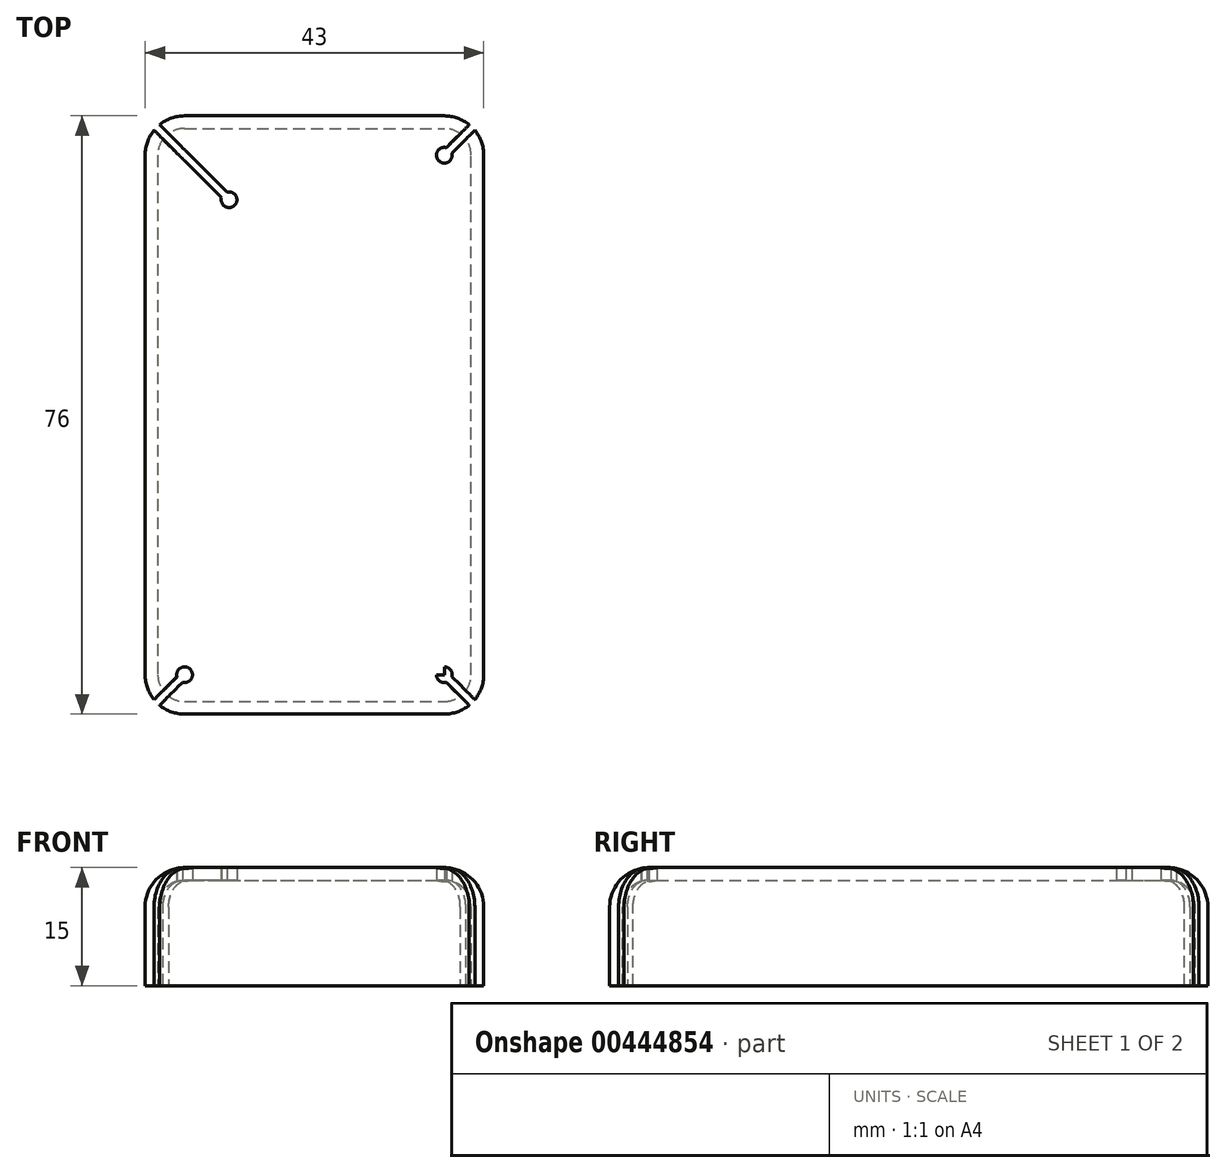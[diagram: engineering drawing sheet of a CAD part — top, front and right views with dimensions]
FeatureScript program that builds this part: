
annotation { "Feature Type Name" : "Feature", "Feature Type Description" : "" }
export const myFeature = defineFeature(function(context is Context, id is Id, definition is map)
    precondition{}
    {
        {
            var Q0;
            Q0=qCreatedBy(makeId("Top.planeOp"),FACE);
            var sketch = newSketch(context, id + "F0", { "sketchPlane" : qUnion([Q0])});
            skLineSegment(sketch, "E0.bottom", {"start": v(-21.5, 38) * mm, "end": v(21.5, 38) * mm});
            skLineSegment(sketch, "E0.top", {"start": v(-21.5, -38) * mm, "end": v(21.5, -38) * mm});
            skLineSegment(sketch, "E0.left", {"start": v(-21.5, 38) * mm, "end": v(-21.5, -38) * mm});
            skLineSegment(sketch, "E0.right", {"start": v(21.5, 38) * mm, "end": v(21.5, -38) * mm});
            skPoint(sketch, "E0.middle", {"position": v(0, 0) * mm});
            skSolve(sketch);
        }
        {
            var Q0;
            Q0=qSketchRegion(id+"F0",true);
            extrude(context, id + "F1", {"entities" : qUnion([Q0]), "depth" : 15 * mm});
        }
        {
            var Q0;
            Q0=makeQuery(id+"F1.opExtrude","SWEPT_EDGE",EDGE,{"disambiguationData":[OSD([sQuery(id+"F0.wireOp",EDGE,"E0.top"),sQuery(id+"F0.wireOp",EDGE,"E0.left")])]});
            var Q1;
            Q1=makeQuery(id+"F1.opExtrude","SWEPT_EDGE",EDGE,{"disambiguationData":[OSD([sQuery(id+"F0.wireOp",EDGE,"E0.top"),sQuery(id+"F0.wireOp",EDGE,"E0.right")])]});
            var Q2;
            Q2=makeQuery(id+"F1.opExtrude","SWEPT_EDGE",EDGE,{"disambiguationData":[OSD([sQuery(id+"F0.wireOp",EDGE,"E0.bottom"),sQuery(id+"F0.wireOp",EDGE,"E0.right")])]});
            var Q3;
            Q3=makeQuery(id+"F1.opExtrude","SWEPT_EDGE",EDGE,{"disambiguationData":[OSD([sQuery(id+"F0.wireOp",EDGE,"E0.bottom"),sQuery(id+"F0.wireOp",EDGE,"E0.left")])]});
            var Q4;
            Q4=makeQuery(id+"F1.opExtrude","CAP_FACE",FACE,{"disambiguationData":[OSD([sQuery(id+"F0.wireOp",EDGE,"E0.bottom"),sQuery(id+"F0.wireOp",EDGE,"E0.top"),sQuery(id+"F0.wireOp",EDGE,"E0.left"),sQuery(id+"F0.wireOp",EDGE,"E0.right")])],"isStart":false});
            fillet(context, id + "F2", {"entities" : qUnion([Q0, Q1, Q2, Q3, Q4]), "radius" : 5 * mm, "tangentPropagation" : true, "allowEdgeOverflow" : false});
        }
        {
            var Q0;
            Q0=makeQuery(id+"F1.opExtrude","CAP_FACE",FACE,{"disambiguationData":[OSD([sQuery(id+"F0.wireOp",EDGE,"E0.bottom"),sQuery(id+"F0.wireOp",EDGE,"E0.top"),sQuery(id+"F0.wireOp",EDGE,"E0.left"),sQuery(id+"F0.wireOp",EDGE,"E0.right")])],"isStart":true});
            shell(context, id + "F3", {"entities" : qUnion([Q0]), "thickness" : 1.6 * mm});
        }
        {
            var Q0;
            Q0=qCreatedBy(makeId("Top.planeOp"),FACE);
            var sketch = newSketch(context, id + "F4", { "sketchPlane" : qUnion([Q0])});
            skLineSegment(sketch, "E1.0.0", {"start": v(-16.5, -33) * mm, "end": v(16.5, -33) * mm});
            skLineSegment(sketch, "E1.0.1", {"start": v(16.5, -33) * mm, "end": v(16.5, 33) * mm});
            skLineSegment(sketch, "E1.0.2", {"start": v(16.5, 33) * mm, "end": v(-16.5, 33) * mm});
            skLineSegment(sketch, "E1.0.3", {"start": v(-16.5, 33) * mm, "end": v(-16.5, -33) * mm});
            skCircle(sketch, "E2", {"center": v(-16.5, -33) * mm, "radius": 1 * mm});
            skCircle(sketch, "E3", {"center": v(16.5, 33) * mm, "radius": 1 * mm});
            skCircle(sketch, "E4", {"center": v(16.5, -33) * mm, "radius": 1 * mm});
            skLineSegment(sketch, "E5", {"start": v(-16.5, 33) * mm, "end": v(-10.84, 27.34) * mm});
            skCircle(sketch, "E6", {"center": v(-10.84, 27.34) * mm, "radius": 1 * mm});
            skPoint(sketch, "E7.0", {"position": v(20.04, 36.54) * mm});
            skLineSegment(sketch, "E8", {"start": v(16.5, 33) * mm, "end": v(20.04, 36.54) * mm});
            skLineSegment(sketch, "E9", {"start": v(20.04, 36.54) * mm, "end": v(19.68, 36.89) * mm});
            skLineSegment(sketch, "E10", {"start": v(19.68, 36.89) * mm, "end": v(15.63, 32.84) * mm});
            skLineSegment(sketch, "E11", {"start": v(20.04, 36.54) * mm, "end": v(20.39, 36.18) * mm});
            skLineSegment(sketch, "E12", {"start": v(20.39, 36.18) * mm, "end": v(16.51, 32.3) * mm});
            skLineSegment(sketch, "E13", {"start": v(16.5, 33) * mm, "end": v(16.85, 32.65) * mm});
            skLineSegment(sketch, "E14", {"start": v(16.5, 33) * mm, "end": v(16.15, 33.35) * mm});
            skPoint(sketch, "E15.0", {"position": v(-20.04, 36.54) * mm});
            skLineSegment(sketch, "E16", {"start": v(-16.5, 33) * mm, "end": v(-20.04, 36.54) * mm});
            skLineSegment(sketch, "E17", {"start": v(-20.04, 36.54) * mm, "end": v(-19.68, 36.89) * mm});
            skLineSegment(sketch, "E18", {"start": v(-19.68, 36.89) * mm, "end": v(-11, 28.2) * mm});
            skLineSegment(sketch, "E19", {"start": v(-20.04, 36.54) * mm, "end": v(-20.39, 36.18) * mm});
            skLineSegment(sketch, "E20", {"start": v(-20.39, 36.18) * mm, "end": v(-11.5, 27.3) * mm});
            skLineSegment(sketch, "E21", {"start": v(-10.84, 27.34) * mm, "end": v(-11.2, 26.99) * mm});
            skLineSegment(sketch, "E22", {"start": v(-10.84, 27.34) * mm, "end": v(-10.49, 27.7) * mm});
            skLineSegment(sketch, "E23.MirrorCS", {"start": v(16.5, -33) * mm, "end": v(16.85, -32.65) * mm});
            skLineSegment(sketch, "E24.MirrorCS", {"start": v(16.5, -33) * mm, "end": v(16.15, -33.35) * mm});
            skLineSegment(sketch, "E25.MirrorCS", {"start": v(20.04, -36.54) * mm, "end": v(20.39, -36.18) * mm});
            skLineSegment(sketch, "E26.MirrorCS", {"start": v(20.04, -36.54) * mm, "end": v(19.68, -36.89) * mm});
            skLineSegment(sketch, "E27.MirrorCS", {"start": v(19.68, -36.89) * mm, "end": v(15.63, -32.84) * mm});
            skPoint(sketch, "E28.MirrorP", {"position": v(20.04, -36.54) * mm});
            skLineSegment(sketch, "E29.MirrorCS", {"start": v(20.39, -36.18) * mm, "end": v(16.51, -32.3) * mm});
            skLineSegment(sketch, "E30.MirrorCS", {"start": v(16.5, -33) * mm, "end": v(20.04, -36.54) * mm});
            skLineSegment(sketch, "E31.MirrorCS", {"start": v(-16.5, -33) * mm, "end": v(-16.85, -32.65) * mm});
            skLineSegment(sketch, "E32.MirrorCS", {"start": v(-16.5, -33) * mm, "end": v(-16.15, -33.35) * mm});
            skLineSegment(sketch, "E33.MirrorCS", {"start": v(-20.04, -36.54) * mm, "end": v(-20.39, -36.18) * mm});
            skLineSegment(sketch, "E34.MirrorCS", {"start": v(-20.04, -36.54) * mm, "end": v(-19.68, -36.89) * mm});
            skLineSegment(sketch, "E35.MirrorCS", {"start": v(-16.5, -33) * mm, "end": v(-16.5, 33) * mm});
            skLineSegment(sketch, "E36.MirrorCS", {"start": v(-20.39, -36.18) * mm, "end": v(-16.51, -32.3) * mm});
            skPoint(sketch, "E37.MirrorP", {"position": v(-20.04, -36.54) * mm});
            skLineSegment(sketch, "E38.MirrorCS", {"start": v(-19.68, -36.89) * mm, "end": v(-15.63, -32.84) * mm});
            skLineSegment(sketch, "E39.MirrorCS", {"start": v(16.5, -33) * mm, "end": v(-16.5, -33) * mm});
            skLineSegment(sketch, "E40.MirrorCS", {"start": v(-16.5, -33) * mm, "end": v(-20.04, -36.54) * mm});
            skSolve(sketch);
        }
        {
            var Q0;
            {var subQ5=sQuery(id+"F4.wireOp",EDGE,"E9");Q0=makeQuery(id+"F4.imprint","IMPRINT",FACE,{"disambiguationData":[TD([[makeQuery(id+"F4.imprint","IMPRINT",EDGE,{"derivedFrom":subQ5}),1.0]])]});}
            var Q1;
            {var subQ5=sQuery(id+"F4.wireOp",EDGE,"E11");Q1=makeQuery(id+"F4.imprint","IMPRINT",FACE,{"disambiguationData":[TD([[makeQuery(id+"F4.imprint","IMPRINT",EDGE,{"derivedFrom":subQ5}),-1.0]])]});}
            var Q2;
            {var subQ0=sQuery(id+"F4.wireOp",EDGE,"E10");var subQ1=sQuery(id+"F4.wireOp",EDGE,"E1.0.2");var subQ2=makeQuery(id+"F4.imprint","INTERSECT",VERTEX,{"derivedFrom":[subQ1,subQ0]});Q2=makeQuery(id+"F4.imprint","IMPRINT",FACE,{"disambiguationData":[TD([[makeQuery(id+"F4.imprint","IMPRINT",EDGE,{"disambiguationData":[TD([[subQ2,-1.0]])],"derivedFrom":subQ1}),-1.0]])]});}
            var Q3;
            {var subQ5=sQuery(id+"F4.wireOp",EDGE,"E14");Q3=makeQuery(id+"F4.imprint","IMPRINT",FACE,{"disambiguationData":[TD([[makeQuery(id+"F4.imprint","IMPRINT",EDGE,{"derivedFrom":subQ5}),-1.0]])]});}
            var Q4;
            {var subQ5=sQuery(id+"F4.wireOp",EDGE,"E13");Q4=makeQuery(id+"F4.imprint","IMPRINT",FACE,{"disambiguationData":[TD([[makeQuery(id+"F4.imprint","IMPRINT",EDGE,{"derivedFrom":subQ5}),1.0]])]});}
            var Q5;
            {var subQ0=sQuery(id+"F4.wireOp",EDGE,"E13");Q5=makeQuery(id+"F4.imprint","IMPRINT",FACE,{"disambiguationData":[TD([[makeQuery(id+"F4.imprint","IMPRINT",EDGE,{"derivedFrom":subQ0}),-1.0]])]});}
            var Q6;
            {var subQ0=sQuery(id+"F4.wireOp",EDGE,"E1.0.2");var subQ5=makeQuery(id+"F4.imprint","INTERSECT",VERTEX,{"derivedFrom":[subQ0,sQuery(id+"F4.wireOp",EDGE,"E10")]});Q6=makeQuery(id+"F4.imprint","IMPRINT",FACE,{"disambiguationData":[TD([[makeQuery(id+"F4.imprint","IMPRINT",EDGE,{"disambiguationData":[TD([[subQ5,-1.0]])],"derivedFrom":subQ0}),1.0]])]});}
            var Q7;
            {var subQ0=sQuery(id+"F4.wireOp",EDGE,"E14");Q7=makeQuery(id+"F4.imprint","IMPRINT",FACE,{"disambiguationData":[TD([[makeQuery(id+"F4.imprint","IMPRINT",EDGE,{"derivedFrom":subQ0}),1.0]])]});}
            var Q8;
            {var subQ0=sQuery(id+"F4.wireOp",EDGE,"E16");Q8=makeQuery(id+"F4.imprint","IMPRINT",FACE,{"disambiguationData":[TD([[makeQuery(id+"F4.imprint","IMPRINT",EDGE,{"derivedFrom":subQ0}),1.0]])]});}
            var Q9;
            {var subQ0=sQuery(id+"F4.wireOp",EDGE,"E16");Q9=makeQuery(id+"F4.imprint","IMPRINT",FACE,{"disambiguationData":[TD([[makeQuery(id+"F4.imprint","IMPRINT",EDGE,{"derivedFrom":subQ0}),-1.0]])]});}
            var Q10;
            {var subQ0=sQuery(id+"F4.wireOp",EDGE,"E5");var subQ5=sQuery(id+"F4.wireOp",EDGE,"E6");var subQ6=makeQuery(id+"F4.imprint","INTERSECT",VERTEX,{"derivedFrom":[subQ0,subQ5]});Q10=makeQuery(id+"F4.imprint","IMPRINT",FACE,{"disambiguationData":[TD([[makeQuery(id+"F4.imprint","IMPRINT",EDGE,{"disambiguationData":[TD([[subQ6,1.0]])],"derivedFrom":subQ5}),-1.0]])]});}
            var Q11;
            {var subQ0=sQuery(id+"F4.wireOp",EDGE,"E5");var subQ5=sQuery(id+"F4.wireOp",EDGE,"E6");var subQ6=makeQuery(id+"F4.imprint","INTERSECT",VERTEX,{"derivedFrom":[subQ0,subQ5]});Q11=makeQuery(id+"F4.imprint","IMPRINT",FACE,{"disambiguationData":[TD([[makeQuery(id+"F4.imprint","IMPRINT",EDGE,{"disambiguationData":[TD([[subQ6,-1.0]])],"derivedFrom":subQ5}),-1.0]])]});}
            var Q12;
            {var subQ0=sQuery(id+"F4.wireOp",EDGE,"E22");Q12=makeQuery(id+"F4.imprint","IMPRINT",FACE,{"disambiguationData":[TD([[makeQuery(id+"F4.imprint","IMPRINT",EDGE,{"derivedFrom":subQ0}),1.0]])]});}
            var Q13;
            {var subQ0=sQuery(id+"F4.wireOp",EDGE,"E18");var subQ1=sQuery(id+"F4.wireOp",EDGE,"E6");var subQ2=makeQuery(id+"F4.imprint","INTERSECT",VERTEX,{"disambiguationData":[OD(0.0)],"derivedFrom":[subQ1,subQ0]});Q13=makeQuery(id+"F4.imprint","IMPRINT",FACE,{"disambiguationData":[TD([[makeQuery(id+"F4.imprint","IMPRINT",EDGE,{"disambiguationData":[TD([[subQ2,-1.0]])],"derivedFrom":subQ1}),1.0]])]});}
            var Q14;
            {var subQ0=sQuery(id+"F4.wireOp",EDGE,"E21");Q14=makeQuery(id+"F4.imprint","IMPRINT",FACE,{"disambiguationData":[TD([[makeQuery(id+"F4.imprint","IMPRINT",EDGE,{"derivedFrom":subQ0}),1.0]])]});}
            var Q15;
            {var subQ0=sQuery(id+"F4.wireOp",EDGE,"E21");Q15=makeQuery(id+"F4.imprint","IMPRINT",FACE,{"disambiguationData":[TD([[makeQuery(id+"F4.imprint","IMPRINT",EDGE,{"derivedFrom":subQ0}),-1.0]])]});}
            var Q16;
            {var subQ0=sQuery(id+"F4.wireOp",EDGE,"E20");var subQ1=sQuery(id+"F4.wireOp",EDGE,"E6");var subQ2=makeQuery(id+"F4.imprint","INTERSECT",VERTEX,{"disambiguationData":[OD(0.0)],"derivedFrom":[subQ1,subQ0]});Q16=makeQuery(id+"F4.imprint","IMPRINT",FACE,{"disambiguationData":[TD([[makeQuery(id+"F4.imprint","IMPRINT",EDGE,{"disambiguationData":[TD([[subQ2,1.0]])],"derivedFrom":subQ1}),1.0]])]});}
            var Q17;
            {var subQ0=sQuery(id+"F4.wireOp",EDGE,"E25.MirrorCS");Q17=makeQuery(id+"F4.imprint","IMPRINT",FACE,{"disambiguationData":[TD([[makeQuery(id+"F4.imprint","IMPRINT",EDGE,{"derivedFrom":subQ0}),1.0]])]});}
            var Q18;
            {var subQ0=sQuery(id+"F4.wireOp",EDGE,"E26.MirrorCS");Q18=makeQuery(id+"F4.imprint","IMPRINT",FACE,{"disambiguationData":[TD([[makeQuery(id+"F4.imprint","IMPRINT",EDGE,{"derivedFrom":subQ0}),-1.0]])]});}
            var Q19;
            {var subQ0=sQuery(id+"F4.wireOp",EDGE,"E24.MirrorCS");Q19=makeQuery(id+"F4.imprint","IMPRINT",FACE,{"disambiguationData":[TD([[makeQuery(id+"F4.imprint","IMPRINT",EDGE,{"derivedFrom":subQ0}),1.0]])]});}
            var Q20;
            {var subQ0=sQuery(id+"F4.wireOp",EDGE,"E23.MirrorCS");Q20=makeQuery(id+"F4.imprint","IMPRINT",FACE,{"disambiguationData":[TD([[makeQuery(id+"F4.imprint","IMPRINT",EDGE,{"derivedFrom":subQ0}),-1.0]])]});}
            var Q21;
            {var subQ0=sQuery(id+"F4.wireOp",EDGE,"E23.MirrorCS");Q21=makeQuery(id+"F4.imprint","IMPRINT",FACE,{"disambiguationData":[TD([[makeQuery(id+"F4.imprint","IMPRINT",EDGE,{"derivedFrom":subQ0}),1.0]])]});}
            var Q22;
            {var subQ1=sQuery(id+"F4.wireOp",EDGE,"E1.0.1");var subQ3=sQuery(id+"F4.wireOp",EDGE,"E4");var subQ4=makeQuery(id+"F4.imprint","INTERSECT",VERTEX,{"derivedFrom":[subQ1,subQ3]});Q22=makeQuery(id+"F4.imprint","IMPRINT",FACE,{"disambiguationData":[TD([[makeQuery(id+"F4.imprint","IMPRINT",EDGE,{"disambiguationData":[TD([[subQ4,1.0]])],"derivedFrom":subQ3}),-1.0]])]});}
            var Q23;
            {var subQ0=sQuery(id+"F4.wireOp",EDGE,"E27.MirrorCS");var subQ1=makeQuery(id+"F4.imprint","INTERSECT",VERTEX,{"derivedFrom":[sQuery(id+"F4.wireOp",EDGE,"E24.MirrorCS"),subQ0]});Q23=makeQuery(id+"F4.imprint","IMPRINT",FACE,{"disambiguationData":[TD([[makeQuery(id+"F4.imprint","IMPRINT",EDGE,{"disambiguationData":[TD([[subQ1,1.0]])],"derivedFrom":subQ0}),1.0]])]});}
            var Q24;
            {var subQ0=sQuery(id+"F4.wireOp",EDGE,"E24.MirrorCS");Q24=makeQuery(id+"F4.imprint","IMPRINT",FACE,{"disambiguationData":[TD([[makeQuery(id+"F4.imprint","IMPRINT",EDGE,{"derivedFrom":subQ0}),-1.0]])]});}
            var Q25;
            {var subQ0=sQuery(id+"F4.wireOp",EDGE,"E39.MirrorCS");var subQ1=sQuery(id+"F4.wireOp",EDGE,"E2");var subQ2=makeQuery(id+"F4.imprint","INTERSECT",VERTEX,{"derivedFrom":[subQ1,subQ0]});Q25=makeQuery(id+"F4.imprint","IMPRINT",FACE,{"disambiguationData":[TD([[makeQuery(id+"F4.imprint","IMPRINT",EDGE,{"disambiguationData":[TD([[subQ2,-1.0]])],"derivedFrom":subQ1}),1.0]])]});}
            var Q26;
            {var subQ0=sQuery(id+"F4.wireOp",EDGE,"E32.MirrorCS");Q26=makeQuery(id+"F4.imprint","IMPRINT",FACE,{"disambiguationData":[TD([[makeQuery(id+"F4.imprint","IMPRINT",EDGE,{"derivedFrom":subQ0}),1.0]])]});}
            var Q27;
            {var subQ0=sQuery(id+"F4.wireOp",EDGE,"E38.MirrorCS");var subQ1=sQuery(id+"F4.wireOp",EDGE,"E2");var subQ2=makeQuery(id+"F4.imprint","INTERSECT",VERTEX,{"derivedFrom":[subQ1,subQ0]});Q27=makeQuery(id+"F4.imprint","IMPRINT",FACE,{"disambiguationData":[TD([[makeQuery(id+"F4.imprint","IMPRINT",EDGE,{"disambiguationData":[TD([[subQ2,-1.0]])],"derivedFrom":subQ1}),1.0]])]});}
            var Q28;
            {var subQ5=sQuery(id+"F4.wireOp",EDGE,"E34.MirrorCS");Q28=makeQuery(id+"F4.imprint","IMPRINT",FACE,{"disambiguationData":[TD([[makeQuery(id+"F4.imprint","IMPRINT",EDGE,{"derivedFrom":subQ5}),1.0]])]});}
            var Q29;
            {var subQ5=sQuery(id+"F4.wireOp",EDGE,"E33.MirrorCS");Q29=makeQuery(id+"F4.imprint","IMPRINT",FACE,{"disambiguationData":[TD([[makeQuery(id+"F4.imprint","IMPRINT",EDGE,{"derivedFrom":subQ5}),-1.0]])]});}
            var Q30;
            {var subQ0=sQuery(id+"F4.wireOp",EDGE,"E31.MirrorCS");Q30=makeQuery(id+"F4.imprint","IMPRINT",FACE,{"disambiguationData":[TD([[makeQuery(id+"F4.imprint","IMPRINT",EDGE,{"derivedFrom":subQ0}),-1.0]])]});}
            var Q31;
            {var subQ0=sQuery(id+"F4.wireOp",EDGE,"E31.MirrorCS");Q31=makeQuery(id+"F4.imprint","IMPRINT",FACE,{"disambiguationData":[TD([[makeQuery(id+"F4.imprint","IMPRINT",EDGE,{"derivedFrom":subQ0}),1.0]])]});}
            var Q32;
            {var subQ5=sQuery(id+"F4.wireOp",EDGE,"E32.MirrorCS");Q32=makeQuery(id+"F4.imprint","IMPRINT",FACE,{"disambiguationData":[TD([[makeQuery(id+"F4.imprint","IMPRINT",EDGE,{"derivedFrom":subQ5}),-1.0]])]});}
            extrude(context, id + "F5", {"entities" : qUnion([Q0, Q1, Q2, Q3, Q4, Q5, Q6, Q7, Q8, Q9, Q10, Q11, Q12, Q13, Q14, Q15, Q16, Q17, Q18, Q19, Q20, Q21, Q22, Q23, Q24, Q25, Q26, Q27, Q28, Q29, Q30, Q31, Q32]), "operationType" : NewBodyOperationType.REMOVE, "depth" : 25 * mm});
        }
    });
